# Revit family: Drain_Fitting_Stainless_Steel_Body_Strainer_Basket-Elkay-LKAD35
name_source: partatom
category: Plumbing Fixtures
units: mm (PartAtom-declared; Revit-internal decimal feet)

## family parameters
Always vertical = Yes
Cut with Voids When Loaded = No
Maintain Annotation Orientation = No
OmniClass Number = 23.45.05.14.14
OmniClass Title = Sinks/Lavatories
Part Type = Normal
Room Calculation Point = No
Round Connector Dimension = Use Diameter
Shared = No
Work Plane-Based = No

## types (1)
- LKAD35 (Drain Fitting" Stainless Steel Body Strainer Basket and Offset and Offset Tailpiece)
    Approx. Shipping Weight (lbs) = 2
    Assembly Code = D2010
    Default Elevation = 0 "
    Description = 3 1/2  Drain Fitting" Stainless Steel Body Strainer Basket and Offset Tailpiece
    Dimensions = 15 13/16 inch x 4 5/8 inch  x 9 1/16 inch
    Manufacturer = Elkay Manufacturer Company
    Manufacturer Brand = Elkay (by Zurn Elkay Water Solutions)
    Model = LKAD35
    Outlet Connection Size (inch) = 1.5 "
    Product Documentation Link = https://www.elkayfiles.com
    Product Installation Sheet URL = https://www.elkayfiles.com
    Product Page URL = https://www.elkay.com
    Product Weight (lbs) = 2
    Product data URL = https://bimobject.com
    Repair Parts URL = https://www.elkayfiles.com
    URL = https://www.elkay.com
    Waste Connection = No

## geometry (parser evidence)
native form markers: Sweep x2
no freeform markers — native parametric forms only
